# Revit family: BTC560
name_source: partatom
category: Structural Connections
revit_build: Autodesk Revit 2014 (Build: 20130308_1515(x64)
units: mm (PartAtom-declared; Revit-internal decimal feet)

## types (1)
- BTC560
    Default Elevation = 0 mm  [stored 0 ft]
    Density = 4.65 kg
    Description = Concealed beam hanger
    EPD = https://www.strongtie.eu
    ETA / DoP = https://www.strongtie.eu
    Manufacturer = Simpson Strong-Tie
    Model = BTC560
    Model Disclaimer = Contact Simpson Strong-Tie Company  for more information
    Model ID = 0309654184424674319918063666023447454145
    Name = BTC560
    ObjectType = BTC560
    Product Material = Galvanised
    Product Type = Concealed beam hanger
    Reference = BTC560-B
    Technical datasheet = https://www.strongtie.eu
    URL = www.strongtie.eu
    UniClass Number = Carbon steel punched metal plate fasteners
    UniClass Title = Pr_20_29_31_13

note: [stored X ft] marks values corroborated as IEEE doubles in the binary element streams (Revit-internal decimal feet)

## geometry (parser evidence)
native form markers: Blend x33, Sweep x1
no freeform markers — native parametric forms only
